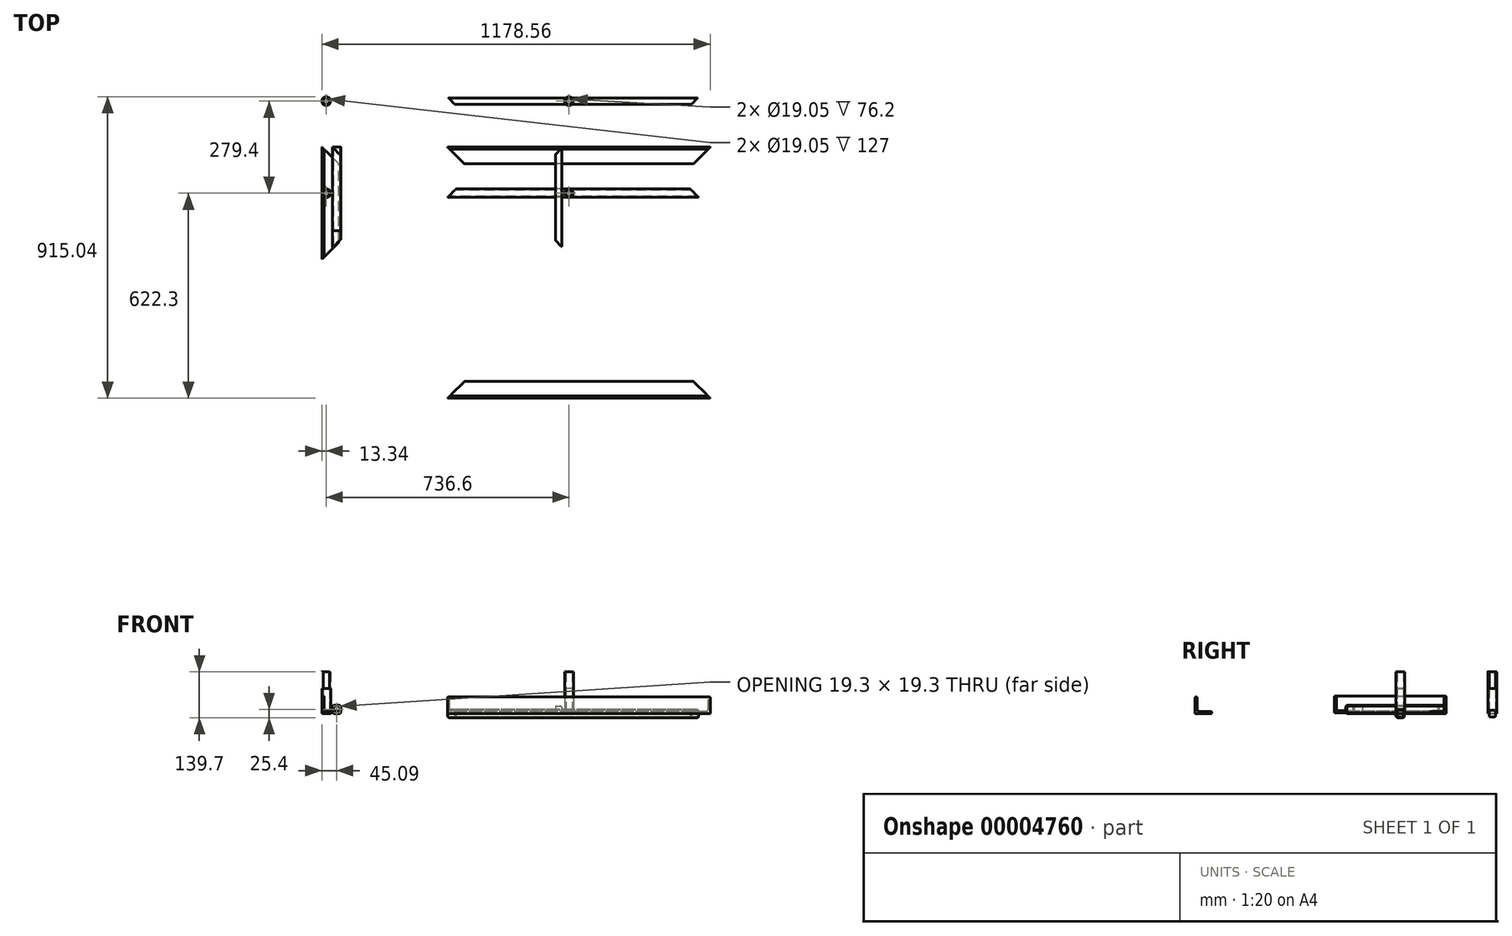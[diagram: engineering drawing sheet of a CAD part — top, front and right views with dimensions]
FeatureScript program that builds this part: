
annotation { "Feature Type Name" : "Feature", "Feature Type Description" : "" }
export const myFeature = defineFeature(function(context is Context, id is Id, definition is map)
    precondition{}
    {
        {
            var Q0;
            Q0=qCreatedBy(makeId("Front.planeOp"),FACE);
            var sketch = newSketch(context, id + "F0", { "sketchPlane" : qUnion([Q0])});
            skLineSegment(sketch, "E0", {"start": v(-381, 50.18) * mm, "end": v(-381, 2.55) * mm});
            skLineSegment(sketch, "E1", {"start": v(-381, 2.55) * mm, "end": v(-333.38, 2.55) * mm});
            skLineSegment(sketch, "E2.0", {"start": v(-368.3, 8.9) * mm, "end": v(-333.38, 8.9) * mm});
            skLineSegment(sketch, "E2.1", {"start": v(-374.65, 50.18) * mm, "end": v(-374.65, 15.25) * mm});
            skArc(sketch, "E3", {"start": v(-374.65, 50.18) * mm, "mid": v(-377.83, 53.35) * mm, "end": v(-381, 50.18) * mm});
            skArc(sketch, "E4", {"start": v(-333.38, 2.55) * mm, "mid": v(-330.2, 5.73) * mm, "end": v(-333.38, 8.9) * mm});
            skPoint(sketch, "E5.visualSharp", {"position": v(-374.65, 8.9) * mm});
            skArc(sketch, "E5.filletArc", {"start": v(-374.65, 15.25) * mm, "mid": v(-372.8, 10.76) * mm, "end": v(-368.3, 8.9) * mm});
            skArc(sketch, "E6.MirrorCS", {"start": v(374.65, 50.18) * mm, "mid": v(377.83, 53.35) * mm, "end": v(381, 50.18) * mm});
            skLineSegment(sketch, "E7.MirrorCS", {"start": v(374.65, 50.18) * mm, "end": v(374.65, 15.25) * mm});
            skArc(sketch, "E8.MirrorCS", {"start": v(374.65, 15.25) * mm, "mid": v(372.8, 10.76) * mm, "end": v(368.3, 8.9) * mm});
            skLineSegment(sketch, "E9.MirrorCS", {"start": v(368.3, 8.9) * mm, "end": v(333.38, 8.9) * mm});
            skArc(sketch, "E10.MirrorCS", {"start": v(333.38, 2.55) * mm, "mid": v(330.2, 5.73) * mm, "end": v(333.38, 8.9) * mm});
            skLineSegment(sketch, "E11.MirrorCS", {"start": v(381, 2.55) * mm, "end": v(333.38, 2.55) * mm});
            skLineSegment(sketch, "E12.MirrorCS", {"start": v(381, 50.18) * mm, "end": v(381, 2.55) * mm});
            skSolve(sketch);
        }
        {
            var Q0;
            Q0=makeQuery(id+"F0.imprint","IMPRINT",FACE,{"disambiguationData":[TD([[makeQuery(id+"F0.imprint","IMPRINT",EDGE,{"derivedFrom":sQuery(id+"F0.wireOp",EDGE,"E6.MirrorCS")}),-1.0]])]});
            var Q1;
            Q1=makeQuery(id+"F0.imprint","IMPRINT",FACE,{"disambiguationData":[TD([[makeQuery(id+"F0.imprint","IMPRINT",EDGE,{"derivedFrom":sQuery(id+"F0.wireOp",EDGE,"E0")}),1.0]])]});
            extrude(context, id + "F1", {"entities" : qUnion([Q0, Q1]), "depth" : 339.72 * mm, "offsetDistance" : 25.4 * mm});
        }
        {
            var Q0;
            Q0=qCreatedBy(makeId("Top.planeOp"),FACE);
            var sketch = newSketch(context, id + "F2", { "sketchPlane" : qUnion([Q0])});
            skLineSegment(sketch, "E13.0", {"start": v(-381, 0) * mm, "end": v(-333.38, 0) * mm});
            skLineSegment(sketch, "E14.0", {"start": v(-381, -339.73) * mm, "end": v(-333.38, -339.73) * mm});
            skLineSegment(sketch, "E15.0", {"start": v(381, -339.73) * mm, "end": v(333.38, -339.73) * mm});
            skLineSegment(sketch, "E16.0", {"start": v(381, 0) * mm, "end": v(333.38, 0) * mm});
            skLineSegment(sketch, "E17", {"start": v(-327.12, -53.88) * mm, "end": v(-381, 0) * mm});
            skLineSegment(sketch, "E18", {"start": v(-327.12, -285.84) * mm, "end": v(-381, -339.73) * mm});
            skLineSegment(sketch, "E19", {"start": v(-333.38, 0) * mm, "end": v(-236.74, 0) * mm});
            skLineSegment(sketch, "E20", {"start": v(-236.74, 0) * mm, "end": v(-327.12, -53.88) * mm});
            skLineSegment(sketch, "E21", {"start": v(-333.38, -339.73) * mm, "end": v(-245.08, -339.73) * mm});
            skLineSegment(sketch, "E22", {"start": v(-245.08, -339.73) * mm, "end": v(-327.12, -285.84) * mm});
            skLineSegment(sketch, "E23", {"start": v(381, 0) * mm, "end": v(311.3, -69.7) * mm});
            skLineSegment(sketch, "E24", {"start": v(381, -339.73) * mm, "end": v(294.62, -253.35) * mm});
            skLineSegment(sketch, "E25", {"start": v(333.38, 0) * mm, "end": v(172.94, 0) * mm});
            skLineSegment(sketch, "E26", {"start": v(172.94, 0) * mm, "end": v(311.3, -69.7) * mm});
            skLineSegment(sketch, "E27", {"start": v(333.38, -339.73) * mm, "end": v(187.89, -339.73) * mm});
            skLineSegment(sketch, "E28", {"start": v(187.89, -339.73) * mm, "end": v(294.62, -253.35) * mm});
            skSolve(sketch);
        }
        {
            var Q0;
            Q0=makeQuery(id+"F2.imprint","IMPRINT",FACE,{"disambiguationData":[TD([[makeQuery(id+"F2.imprint","IMPRINT",EDGE,{"derivedFrom":sQuery(id+"F2.wireOp",EDGE,"E14.0")}),1.0]])]});
            var Q1;
            Q1=makeQuery(id+"F2.imprint","IMPRINT",FACE,{"disambiguationData":[TD([[makeQuery(id+"F2.imprint","IMPRINT",EDGE,{"derivedFrom":sQuery(id+"F2.wireOp",EDGE,"E13.0")}),-1.0]])]});
            var Q2;
            Q2=makeQuery(id+"F2.imprint","IMPRINT",FACE,{"disambiguationData":[TD([[makeQuery(id+"F2.imprint","IMPRINT",EDGE,{"derivedFrom":sQuery(id+"F2.wireOp",EDGE,"E16.0")}),1.0]])]});
            var Q3;
            Q3=makeQuery(id+"F2.imprint","IMPRINT",FACE,{"disambiguationData":[TD([[makeQuery(id+"F2.imprint","IMPRINT",EDGE,{"derivedFrom":sQuery(id+"F2.wireOp",EDGE,"E15.0")}),-1.0]])]});
            extrude(context, id + "F3", {"entities" : qUnion([Q0, Q1, Q2, Q3]), "depth" : 76.2 * mm, "offsetDistance" : 25.4 * mm});
        }
        {
            var Q0;
            Q0=makeQuery(id+"F3.opExtrude","SWEPT_BODY",BODY,{"disambiguationData":[OSD([sQuery(id+"F2.wireOp",EDGE,"E13.0"),sQuery(id+"F2.wireOp",EDGE,"E17"),sQuery(id+"F2.wireOp",EDGE,"E19"),sQuery(id+"F2.wireOp",EDGE,"E20")])]});
            var Q1;
            Q1=makeQuery(id+"F3.opExtrude","SWEPT_BODY",BODY,{"disambiguationData":[OSD([sQuery(id+"F2.wireOp",EDGE,"E14.0"),sQuery(id+"F2.wireOp",EDGE,"E18"),sQuery(id+"F2.wireOp",EDGE,"E21"),sQuery(id+"F2.wireOp",EDGE,"E22")])]});
            var Q2;
            Q2=makeQuery(id+"F3.opExtrude","SWEPT_BODY",BODY,{"disambiguationData":[OSD([sQuery(id+"F2.wireOp",EDGE,"E16.0"),sQuery(id+"F2.wireOp",EDGE,"E23"),sQuery(id+"F2.wireOp",EDGE,"E25"),sQuery(id+"F2.wireOp",EDGE,"E26")])]});
            var Q3;
            Q3=makeQuery(id+"F3.opExtrude","SWEPT_BODY",BODY,{"disambiguationData":[OSD([sQuery(id+"F2.wireOp",EDGE,"E15.0"),sQuery(id+"F2.wireOp",EDGE,"E24"),sQuery(id+"F2.wireOp",EDGE,"E27"),sQuery(id+"F2.wireOp",EDGE,"E28")])]});
            var Q4;
            Q4=makeQuery(id+"F1.opExtrude","SWEPT_BODY",BODY,{"disambiguationData":[OSD([sQuery(id+"F0.wireOp",EDGE,"E0"),sQuery(id+"F0.wireOp",EDGE,"E1"),sQuery(id+"F0.wireOp",EDGE,"E2.0"),sQuery(id+"F0.wireOp",EDGE,"E2.1"),sQuery(id+"F0.wireOp",EDGE,"E3"),sQuery(id+"F0.wireOp",EDGE,"E4"),sQuery(id+"F0.wireOp",EDGE,"E5.filletArc")])]});
            var Q5;
            Q5=makeQuery(id+"F1.opExtrude","SWEPT_BODY",BODY,{"disambiguationData":[OSD([sQuery(id+"F0.wireOp",EDGE,"E6.MirrorCS"),sQuery(id+"F0.wireOp",EDGE,"E7.MirrorCS"),sQuery(id+"F0.wireOp",EDGE,"E8.MirrorCS"),sQuery(id+"F0.wireOp",EDGE,"E9.MirrorCS"),sQuery(id+"F0.wireOp",EDGE,"E10.MirrorCS"),sQuery(id+"F0.wireOp",EDGE,"E11.MirrorCS"),sQuery(id+"F0.wireOp",EDGE,"E12.MirrorCS")])]});
            booleanBodies(context, id + "F4", {"operationType" : BooleanOperationType.SUBTRACTION, "tools" : qUnion([Q0, Q1, Q2, Q3]), "targets" : qUnion([Q4, Q5])});
        }
        {
            var Q0;
            Q0=qCreatedBy(makeId("Right.planeOp"),FACE);
            var sketch = newSketch(context, id + "F5", { "sketchPlane" : qUnion([Q0])});
            skLineSegment(sketch, "E29", {"start": v(-762, 47.62) * mm, "end": v(-762, 0) * mm});
            skLineSegment(sketch, "E30", {"start": v(-762, 0) * mm, "end": v(-714.38, 0) * mm});
            skLineSegment(sketch, "E31.0", {"start": v(-749.3, 6.35) * mm, "end": v(-714.38, 6.35) * mm});
            skLineSegment(sketch, "E31.1", {"start": v(-755.65, 47.62) * mm, "end": v(-755.65, 12.7) * mm});
            skArc(sketch, "E32", {"start": v(-755.65, 47.62) * mm, "mid": v(-758.83, 50.8) * mm, "end": v(-762, 47.62) * mm});
            skArc(sketch, "E33", {"start": v(-714.38, 0) * mm, "mid": v(-711.2, 3.17) * mm, "end": v(-714.38, 6.35) * mm});
            skPoint(sketch, "E34.visualSharp", {"position": v(-755.65, 6.35) * mm});
            skArc(sketch, "E34.filletArc", {"start": v(-755.65, 12.7) * mm, "mid": v(-753.8, 8.2) * mm, "end": v(-749.3, 6.35) * mm});
            skLineSegment(sketch, "E35", {"start": v(-47.63, 0) * mm, "end": v(0, 0) * mm});
            skLineSegment(sketch, "E36", {"start": v(0, 0) * mm, "end": v(0, 47.62) * mm});
            skLineSegment(sketch, "E37.0", {"start": v(-6.35, 12.7) * mm, "end": v(-6.35, 47.62) * mm});
            skLineSegment(sketch, "E37.1", {"start": v(-47.63, 6.35) * mm, "end": v(-12.7, 6.35) * mm});
            skArc(sketch, "E38", {"start": v(-47.63, 6.35) * mm, "mid": v(-50.8, 3.17) * mm, "end": v(-47.63, 0) * mm});
            skArc(sketch, "E39", {"start": v(0, 47.62) * mm, "mid": v(-3.18, 50.8) * mm, "end": v(-6.35, 47.62) * mm});
            skPoint(sketch, "E40.visualSharp", {"position": v(-6.35, 6.35) * mm});
            skArc(sketch, "E40.filletArc", {"start": v(-12.7, 6.35) * mm, "mid": v(-8.2, 8.2) * mm, "end": v(-6.35, 12.7) * mm});
            skSolve(sketch);
        }
        {
            var Q0;
            Q0=makeQuery(id+"F5.imprint","IMPRINT",FACE,{"disambiguationData":[TD([[makeQuery(id+"F5.imprint","IMPRINT",EDGE,{"derivedFrom":sQuery(id+"F5.wireOp",EDGE,"E29")}),1.0]])]});
            var Q1;
            Q1=makeQuery(id+"F5.imprint","IMPRINT",FACE,{"disambiguationData":[TD([[makeQuery(id+"F5.imprint","IMPRINT",EDGE,{"derivedFrom":sQuery(id+"F5.wireOp",EDGE,"E35")}),1.0]])]});
            extrude(context, id + "F6", {"entities" : qUnion([Q0, Q1]), "depth" : 796.92 * mm, "offsetDistance" : 25.4 * mm});
        }
        {
            var Q0;
            Q0=qCreatedBy(makeId("Top.planeOp"),FACE);
            var sketch = newSketch(context, id + "F7", { "sketchPlane" : qUnion([Q0])});
            skLineSegment(sketch, "E41.0", {"start": v(796.93, -47.63) * mm, "end": v(796.93, 0) * mm});
            skLineSegment(sketch, "E42.0", {"start": v(796.93, -762) * mm, "end": v(796.93, -714.38) * mm});
            skLineSegment(sketch, "E43.0", {"start": v(0, -762) * mm, "end": v(0, -714.38) * mm});
            skLineSegment(sketch, "E44.0", {"start": v(0, -47.63) * mm, "end": v(0, 0) * mm});
            skLineSegment(sketch, "E45", {"start": v(0, 0) * mm, "end": v(70.95, -70.95) * mm});
            skLineSegment(sketch, "E46", {"start": v(796.93, 0) * mm, "end": v(711.06, -85.86) * mm});
            skLineSegment(sketch, "E47", {"start": v(0, -47.63) * mm, "end": v(0, -70.95) * mm});
            skLineSegment(sketch, "E48", {"start": v(0, -70.95) * mm, "end": v(70.95, -70.95) * mm});
            skLineSegment(sketch, "E49", {"start": v(796.93, -47.63) * mm, "end": v(796.93, -85.86) * mm});
            skLineSegment(sketch, "E50", {"start": v(796.93, -85.86) * mm, "end": v(711.06, -85.86) * mm});
            skLineSegment(sketch, "E51", {"start": v(0, -762) * mm, "end": v(84.63, -677.37) * mm});
            skLineSegment(sketch, "E52", {"start": v(796.93, -762) * mm, "end": v(712.97, -678.04) * mm});
            skLineSegment(sketch, "E53", {"start": v(0, -714.38) * mm, "end": v(0, -677.37) * mm});
            skLineSegment(sketch, "E54", {"start": v(0, -677.37) * mm, "end": v(84.63, -677.37) * mm});
            skLineSegment(sketch, "E55", {"start": v(796.93, -714.38) * mm, "end": v(796.93, -678.04) * mm});
            skLineSegment(sketch, "E56", {"start": v(796.93, -678.04) * mm, "end": v(712.97, -678.04) * mm});
            skSolve(sketch);
        }
        {
            var Q0;
            Q0=makeQuery(id+"F7.imprint","IMPRINT",FACE,{"disambiguationData":[TD([[makeQuery(id+"F7.imprint","IMPRINT",EDGE,{"derivedFrom":sQuery(id+"F7.wireOp",EDGE,"E44.0")}),-1.0]])]});
            var Q1;
            Q1=makeQuery(id+"F7.imprint","IMPRINT",FACE,{"disambiguationData":[TD([[makeQuery(id+"F7.imprint","IMPRINT",EDGE,{"derivedFrom":sQuery(id+"F7.wireOp",EDGE,"E41.0")}),1.0]])]});
            var Q2;
            Q2=makeQuery(id+"F7.imprint","IMPRINT",FACE,{"disambiguationData":[TD([[makeQuery(id+"F7.imprint","IMPRINT",EDGE,{"derivedFrom":sQuery(id+"F7.wireOp",EDGE,"E43.0")}),-1.0]])]});
            var Q3;
            Q3=makeQuery(id+"F7.imprint","IMPRINT",FACE,{"disambiguationData":[TD([[makeQuery(id+"F7.imprint","IMPRINT",EDGE,{"derivedFrom":sQuery(id+"F7.wireOp",EDGE,"E42.0")}),1.0]])]});
            extrude(context, id + "F8", {"entities" : qUnion([Q0, Q1, Q2, Q3]), "depth" : 76.2 * mm, "offsetDistance" : 25.4 * mm});
        }
        {
            var Q0;
            Q0=makeQuery(id+"F8.opExtrude","SWEPT_BODY",BODY,{"disambiguationData":[OSD([sQuery(id+"F7.wireOp",EDGE,"E44.0"),sQuery(id+"F7.wireOp",EDGE,"E45"),sQuery(id+"F7.wireOp",EDGE,"E47"),sQuery(id+"F7.wireOp",EDGE,"E48")])]});
            var Q1;
            Q1=makeQuery(id+"F8.opExtrude","SWEPT_BODY",BODY,{"disambiguationData":[OSD([sQuery(id+"F7.wireOp",EDGE,"E41.0"),sQuery(id+"F7.wireOp",EDGE,"E46"),sQuery(id+"F7.wireOp",EDGE,"E49"),sQuery(id+"F7.wireOp",EDGE,"E50")])]});
            var Q2;
            Q2=makeQuery(id+"F8.opExtrude","SWEPT_BODY",BODY,{"disambiguationData":[OSD([sQuery(id+"F7.wireOp",EDGE,"E43.0"),sQuery(id+"F7.wireOp",EDGE,"E51"),sQuery(id+"F7.wireOp",EDGE,"E53"),sQuery(id+"F7.wireOp",EDGE,"E54")])]});
            var Q3;
            Q3=makeQuery(id+"F8.opExtrude","SWEPT_BODY",BODY,{"disambiguationData":[OSD([sQuery(id+"F7.wireOp",EDGE,"E42.0"),sQuery(id+"F7.wireOp",EDGE,"E52"),sQuery(id+"F7.wireOp",EDGE,"E55"),sQuery(id+"F7.wireOp",EDGE,"E56")])]});
            var Q4;
            Q4=makeQuery(id+"F6.opExtrude","SWEPT_BODY",BODY,{"disambiguationData":[OSD([sQuery(id+"F5.wireOp",EDGE,"E35"),sQuery(id+"F5.wireOp",EDGE,"E36"),sQuery(id+"F5.wireOp",EDGE,"E37.0"),sQuery(id+"F5.wireOp",EDGE,"E37.1"),sQuery(id+"F5.wireOp",EDGE,"E38"),sQuery(id+"F5.wireOp",EDGE,"E39"),sQuery(id+"F5.wireOp",EDGE,"E40.filletArc")])]});
            var Q5;
            Q5=makeQuery(id+"F6.opExtrude","SWEPT_BODY",BODY,{"disambiguationData":[OSD([sQuery(id+"F5.wireOp",EDGE,"E29"),sQuery(id+"F5.wireOp",EDGE,"E30"),sQuery(id+"F5.wireOp",EDGE,"E31.0"),sQuery(id+"F5.wireOp",EDGE,"E31.1"),sQuery(id+"F5.wireOp",EDGE,"E32"),sQuery(id+"F5.wireOp",EDGE,"E33"),sQuery(id+"F5.wireOp",EDGE,"E34.filletArc")])]});
            booleanBodies(context, id + "F9", {"operationType" : BooleanOperationType.SUBTRACTION, "tools" : qUnion([Q0, Q1, Q2, Q3]), "targets" : qUnion([Q4, Q5])});
        }
        {
            var Q0;
            Q0=qCreatedBy(makeId("Front.planeOp"),FACE);
            var sketch = newSketch(context, id + "F10", { "sketchPlane" : qUnion([Q0])});
            skLineSegment(sketch, "E57.bottom", {"start": v(-329.95, 25.4) * mm, "end": v(-343.15, 25.4) * mm});
            skLineSegment(sketch, "E57.top", {"start": v(-329.95, 0) * mm, "end": v(-343.15, 0) * mm});
            skLineSegment(sketch, "E57.left", {"start": v(-323.85, 19.3) * mm, "end": v(-323.85, 6.1) * mm});
            skLineSegment(sketch, "E57.right", {"start": v(-349.25, 19.3) * mm, "end": v(-349.25, 6.1) * mm});
            skPoint(sketch, "E57.middle", {"position": v(-336.55, 12.7) * mm});
            skPoint(sketch, "E58.visualSharp", {"position": v(-349.25, 25.4) * mm});
            skArc(sketch, "E58.filletArc", {"start": v(-343.15, 25.4) * mm, "mid": v(-347.46, 23.61) * mm, "end": v(-349.25, 19.3) * mm});
            skPoint(sketch, "E59.visualSharp", {"position": v(-323.85, 25.4) * mm});
            skArc(sketch, "E59.filletArc", {"start": v(-323.85, 19.3) * mm, "mid": v(-325.64, 23.61) * mm, "end": v(-329.95, 25.4) * mm});
            skPoint(sketch, "E60.visualSharp", {"position": v(-323.85, 0) * mm});
            skArc(sketch, "E60.filletArc", {"start": v(-329.95, 0) * mm, "mid": v(-325.64, 1.79) * mm, "end": v(-323.85, 6.1) * mm});
            skPoint(sketch, "E61.visualSharp", {"position": v(-349.25, 0) * mm});
            skArc(sketch, "E61.filletArc", {"start": v(-349.25, 6.1) * mm, "mid": v(-347.46, 1.79) * mm, "end": v(-343.15, 0) * mm});
            skArc(sketch, "E62.0", {"start": v(-326.9, 19.3) * mm, "mid": v(-327.8, 21.46) * mm, "end": v(-329.95, 22.35) * mm});
            skLineSegment(sketch, "E62.1", {"start": v(-326.9, 19.3) * mm, "end": v(-326.9, 6.1) * mm});
            skLineSegment(sketch, "E62.2", {"start": v(-329.95, 22.35) * mm, "end": v(-343.15, 22.35) * mm});
            skArc(sketch, "E62.3", {"start": v(-329.95, 3.05) * mm, "mid": v(-327.8, 3.94) * mm, "end": v(-326.9, 6.1) * mm});
            skArc(sketch, "E62.4", {"start": v(-343.15, 22.35) * mm, "mid": v(-345.3, 21.46) * mm, "end": v(-346.2, 19.3) * mm});
            skLineSegment(sketch, "E62.5", {"start": v(-346.2, 19.3) * mm, "end": v(-346.2, 6.1) * mm});
            skArc(sketch, "E62.6", {"start": v(-346.2, 6.1) * mm, "mid": v(-345.3, 3.94) * mm, "end": v(-343.15, 3.05) * mm});
            skLineSegment(sketch, "E62.7", {"start": v(-329.95, 3.05) * mm, "end": v(-343.15, 3.05) * mm});
            skLineSegment(sketch, "E63", {"start": v(0, 42.38) * mm, "end": v(0, -25.41) * mm});
            skPoint(sketch, "E64", {"position": v(0, 0) * mm});
            skArc(sketch, "E65.MirrorCS", {"start": v(346.2, 6.1) * mm, "mid": v(345.3, 3.94) * mm, "end": v(343.15, 3.05) * mm});
            skArc(sketch, "E66.MirrorCS", {"start": v(329.95, 3.05) * mm, "mid": v(327.8, 3.94) * mm, "end": v(326.9, 6.1) * mm});
            skArc(sketch, "E67.MirrorCS", {"start": v(326.9, 19.3) * mm, "mid": v(327.8, 21.46) * mm, "end": v(329.95, 22.35) * mm});
            skArc(sketch, "E68.MirrorCS", {"start": v(343.15, 22.35) * mm, "mid": v(345.3, 21.46) * mm, "end": v(346.2, 19.3) * mm});
            skArc(sketch, "E69.MirrorCS", {"start": v(323.85, 19.3) * mm, "mid": v(325.64, 23.61) * mm, "end": v(329.95, 25.4) * mm});
            skLineSegment(sketch, "E70.MirrorCS", {"start": v(329.95, 22.35) * mm, "end": v(343.15, 22.35) * mm});
            skLineSegment(sketch, "E71.MirrorCS", {"start": v(329.95, 25.4) * mm, "end": v(343.15, 25.4) * mm});
            skArc(sketch, "E72.MirrorCS", {"start": v(349.25, 6.1) * mm, "mid": v(347.46, 1.79) * mm, "end": v(343.15, 0) * mm});
            skLineSegment(sketch, "E73.MirrorCS", {"start": v(329.95, 3.05) * mm, "end": v(343.15, 3.05) * mm});
            skArc(sketch, "E74.MirrorCS", {"start": v(329.95, 0) * mm, "mid": v(325.64, 1.79) * mm, "end": v(323.85, 6.1) * mm});
            skArc(sketch, "E75.MirrorCS", {"start": v(343.15, 25.4) * mm, "mid": v(347.46, 23.61) * mm, "end": v(349.25, 19.3) * mm});
            skLineSegment(sketch, "E76.MirrorCS", {"start": v(329.95, 0) * mm, "end": v(343.15, 0) * mm});
            skPoint(sketch, "E77.MirrorP", {"position": v(349.25, 0) * mm});
            skLineSegment(sketch, "E78.MirrorCS", {"start": v(349.25, 19.3) * mm, "end": v(349.25, 6.1) * mm});
            skPoint(sketch, "E79.MirrorP", {"position": v(336.55, 12.7) * mm});
            skLineSegment(sketch, "E80.MirrorCS", {"start": v(346.2, 19.3) * mm, "end": v(346.2, 6.1) * mm});
            skLineSegment(sketch, "E81.MirrorCS", {"start": v(323.85, 19.3) * mm, "end": v(323.85, 6.1) * mm});
            skPoint(sketch, "E82.MirrorP", {"position": v(323.85, 0) * mm});
            skLineSegment(sketch, "E83.MirrorCS", {"start": v(326.9, 19.3) * mm, "end": v(326.9, 6.1) * mm});
            skPoint(sketch, "E84.MirrorP", {"position": v(349.25, 25.4) * mm});
            skPoint(sketch, "E85.MirrorP", {"position": v(323.85, 25.4) * mm});
            skSolve(sketch);
        }
        {
            var Q0;
            Q0=makeQuery(id+"F10.imprint","IMPRINT",FACE,{"disambiguationData":[TD([[makeQuery(id+"F10.imprint","IMPRINT",EDGE,{"derivedFrom":sQuery(id+"F10.wireOp",EDGE,"E57.bottom")}),1.0]])]});
            var Q1;
            Q1=makeQuery(id+"F10.imprint","IMPRINT",FACE,{"disambiguationData":[TD([[makeQuery(id+"F10.imprint","IMPRINT",EDGE,{"derivedFrom":sQuery(id+"F10.wireOp",EDGE,"E65.MirrorCS")}),1.0]])]});
            extrude(context, id + "F11", {"entities" : qUnion([Q0, Q1]), "depth" : 304.8 * mm, "offsetDistance" : 25.4 * mm});
        }
        {
            var Q0;
            Q0=qCreatedBy(makeId("Top.planeOp"),FACE);
            var sketch = newSketch(context, id + "F12", { "sketchPlane" : qUnion([Q0])});
            skLineSegment(sketch, "E86.0", {"start": v(-323.85, -304.8) * mm, "end": v(-349.25, -304.8) * mm});
            skLineSegment(sketch, "E86.1", {"start": v(-349.25, -304.8) * mm, "end": v(-323.85, -279.4) * mm});
            skLineSegment(sketch, "E86.2", {"start": v(-323.85, -279.4) * mm, "end": v(-323.85, -304.8) * mm});
            skPoint(sketch, "E86.0.midPoint", {"position": v(-336.55, -304.8) * mm});
            skPoint(sketch, "E87", {"position": v(-323.85, -292.1) * mm});
            skLineSegment(sketch, "E88.0", {"start": v(-323.85, 0) * mm, "end": v(-323.85, -25.4) * mm});
            skLineSegment(sketch, "E88.1", {"start": v(-323.85, -25.4) * mm, "end": v(-349.25, 0) * mm});
            skLineSegment(sketch, "E88.2", {"start": v(-349.25, 0) * mm, "end": v(-323.85, 0) * mm});
            skPoint(sketch, "E88.0.midPoint", {"position": v(-323.85, -12.7) * mm});
            skPoint(sketch, "E89", {"position": v(-336.55, 0) * mm});
            skLineSegment(sketch, "E90.MirrorCS", {"start": v(323.85, 0) * mm, "end": v(323.85, -25.4) * mm});
            skLineSegment(sketch, "E91.MirrorCS", {"start": v(323.85, -304.8) * mm, "end": v(349.25, -304.8) * mm});
            skLineSegment(sketch, "E92.MirrorCS", {"start": v(323.85, -279.4) * mm, "end": v(323.85, -304.8) * mm});
            skLineSegment(sketch, "E93.MirrorCS", {"start": v(349.25, 0) * mm, "end": v(323.85, 0) * mm});
            skPoint(sketch, "E94.MirrorP", {"position": v(323.85, -12.7) * mm});
            skPoint(sketch, "E95.MirrorP", {"position": v(323.85, -292.1) * mm});
            skLineSegment(sketch, "E96.MirrorCS", {"start": v(323.85, -25.4) * mm, "end": v(349.25, 0) * mm});
            skPoint(sketch, "E97.MirrorP", {"position": v(336.55, 0) * mm});
            skLineSegment(sketch, "E98.MirrorCS", {"start": v(349.25, -304.8) * mm, "end": v(323.85, -279.4) * mm});
            skPoint(sketch, "E99.MirrorP", {"position": v(336.55, -304.8) * mm});
            skSolve(sketch);
        }
        {
            var Q0;
            Q0=makeQuery(id+"F12.imprint","IMPRINT",FACE,{"disambiguationData":[TD([[makeQuery(id+"F12.imprint","IMPRINT",EDGE,{"derivedFrom":sQuery(id+"F12.wireOp",EDGE,"E86.0")}),-1.0]])]});
            var Q1;
            Q1=makeQuery(id+"F12.imprint","IMPRINT",FACE,{"disambiguationData":[TD([[makeQuery(id+"F12.imprint","IMPRINT",EDGE,{"derivedFrom":sQuery(id+"F12.wireOp",EDGE,"E91.MirrorCS")}),1.0]])]});
            var Q2;
            Q2=makeQuery(id+"F12.imprint","IMPRINT",FACE,{"disambiguationData":[TD([[makeQuery(id+"F12.imprint","IMPRINT",EDGE,{"derivedFrom":sQuery(id+"F12.wireOp",EDGE,"E90.MirrorCS")}),1.0]])]});
            var Q3;
            Q3=makeQuery(id+"F12.imprint","IMPRINT",FACE,{"disambiguationData":[TD([[makeQuery(id+"F12.imprint","IMPRINT",EDGE,{"derivedFrom":sQuery(id+"F12.wireOp",EDGE,"E88.0")}),-1.0]])]});
            extrude(context, id + "F13", {"entities" : qUnion([Q0, Q1, Q2, Q3]), "depth" : 76.2 * mm, "offsetDistance" : 25.4 * mm});
        }
        {
            var Q0;
            Q0=makeQuery(id+"F13.opExtrude","SWEPT_BODY",BODY,{"disambiguationData":[OSD([sQuery(id+"F12.wireOp",EDGE,"E90.MirrorCS"),sQuery(id+"F12.wireOp",EDGE,"E93.MirrorCS"),sQuery(id+"F12.wireOp",EDGE,"E96.MirrorCS")])]});
            var Q1;
            Q1=makeQuery(id+"F13.opExtrude","SWEPT_BODY",BODY,{"disambiguationData":[OSD([sQuery(id+"F12.wireOp",EDGE,"E91.MirrorCS"),sQuery(id+"F12.wireOp",EDGE,"E92.MirrorCS"),sQuery(id+"F12.wireOp",EDGE,"E98.MirrorCS")])]});
            var Q2;
            Q2=makeQuery(id+"F13.opExtrude","SWEPT_BODY",BODY,{"disambiguationData":[OSD([sQuery(id+"F12.wireOp",EDGE,"E86.0"),sQuery(id+"F12.wireOp",EDGE,"E86.1"),sQuery(id+"F12.wireOp",EDGE,"E86.2")])]});
            var Q3;
            Q3=makeQuery(id+"F13.opExtrude","SWEPT_BODY",BODY,{"disambiguationData":[OSD([sQuery(id+"F12.wireOp",EDGE,"E88.0"),sQuery(id+"F12.wireOp",EDGE,"E88.1"),sQuery(id+"F12.wireOp",EDGE,"E88.2")])]});
            var Q4;
            Q4=makeQuery(id+"F11.opExtrude","SWEPT_BODY",BODY,{"disambiguationData":[OSD([sQuery(id+"F10.wireOp",EDGE,"E57.bottom"),sQuery(id+"F10.wireOp",EDGE,"E57.top"),sQuery(id+"F10.wireOp",EDGE,"E57.left"),sQuery(id+"F10.wireOp",EDGE,"E57.right"),sQuery(id+"F10.wireOp",EDGE,"E58.filletArc"),sQuery(id+"F10.wireOp",EDGE,"E59.filletArc"),sQuery(id+"F10.wireOp",EDGE,"E60.filletArc"),sQuery(id+"F10.wireOp",EDGE,"E61.filletArc"),sQuery(id+"F10.wireOp",EDGE,"E62.0"),sQuery(id+"F10.wireOp",EDGE,"E62.1"),sQuery(id+"F10.wireOp",EDGE,"E62.2"),sQuery(id+"F10.wireOp",EDGE,"E62.3"),sQuery(id+"F10.wireOp",EDGE,"E62.4"),sQuery(id+"F10.wireOp",EDGE,"E62.5"),sQuery(id+"F10.wireOp",EDGE,"E62.6"),sQuery(id+"F10.wireOp",EDGE,"E62.7")])]});
            var Q5;
            Q5=makeQuery(id+"F11.opExtrude","SWEPT_BODY",BODY,{"disambiguationData":[OSD([sQuery(id+"F10.wireOp",EDGE,"E65.MirrorCS"),sQuery(id+"F10.wireOp",EDGE,"E66.MirrorCS"),sQuery(id+"F10.wireOp",EDGE,"E67.MirrorCS"),sQuery(id+"F10.wireOp",EDGE,"E68.MirrorCS"),sQuery(id+"F10.wireOp",EDGE,"E69.MirrorCS"),sQuery(id+"F10.wireOp",EDGE,"E70.MirrorCS"),sQuery(id+"F10.wireOp",EDGE,"E71.MirrorCS"),sQuery(id+"F10.wireOp",EDGE,"E72.MirrorCS"),sQuery(id+"F10.wireOp",EDGE,"E73.MirrorCS"),sQuery(id+"F10.wireOp",EDGE,"E74.MirrorCS"),sQuery(id+"F10.wireOp",EDGE,"E75.MirrorCS"),sQuery(id+"F10.wireOp",EDGE,"E76.MirrorCS"),sQuery(id+"F10.wireOp",EDGE,"E78.MirrorCS"),sQuery(id+"F10.wireOp",EDGE,"E80.MirrorCS"),sQuery(id+"F10.wireOp",EDGE,"E81.MirrorCS"),sQuery(id+"F10.wireOp",EDGE,"E83.MirrorCS")])]});
            booleanBodies(context, id + "F14", {"operationType" : BooleanOperationType.SUBTRACTION, "tools" : qUnion([Q0, Q1, Q2, Q3]), "targets" : qUnion([Q4, Q5])});
        }
        {
            var Q0;
            Q0=qCreatedBy(makeId("Right.planeOp"),FACE);
            var sketch = newSketch(context, id + "F15", { "sketchPlane" : qUnion([Q0])});
            skLineSegment(sketch, "E100.bottom", {"start": v(-133.1, 12.7) * mm, "end": v(-146.3, 12.7) * mm});
            skLineSegment(sketch, "E100.top", {"start": v(-133.1, -12.7) * mm, "end": v(-146.3, -12.7) * mm});
            skLineSegment(sketch, "E100.left", {"start": v(-127, 6.6) * mm, "end": v(-127, -6.6) * mm});
            skLineSegment(sketch, "E100.right", {"start": v(-152.4, 6.6) * mm, "end": v(-152.4, -6.6) * mm});
            skPoint(sketch, "E100.middle", {"position": v(-139.7, 0) * mm});
            skPoint(sketch, "E101.visualSharp", {"position": v(-152.4, 12.7) * mm});
            skArc(sketch, "E101.filletArc", {"start": v(-146.3, 12.7) * mm, "mid": v(-150.61, 10.91) * mm, "end": v(-152.4, 6.6) * mm});
            skPoint(sketch, "E102.visualSharp", {"position": v(-127, 12.7) * mm});
            skArc(sketch, "E102.filletArc", {"start": v(-127, 6.6) * mm, "mid": v(-128.79, 10.91) * mm, "end": v(-133.1, 12.7) * mm});
            skPoint(sketch, "E103.visualSharp", {"position": v(-127, -12.7) * mm});
            skArc(sketch, "E103.filletArc", {"start": v(-133.1, -12.7) * mm, "mid": v(-128.79, -10.91) * mm, "end": v(-127, -6.6) * mm});
            skPoint(sketch, "E104.visualSharp", {"position": v(-152.4, -12.7) * mm});
            skArc(sketch, "E104.filletArc", {"start": v(-152.4, -6.6) * mm, "mid": v(-150.61, -10.91) * mm, "end": v(-146.3, -12.7) * mm});
            skArc(sketch, "E105.0", {"start": v(-130.05, 6.6) * mm, "mid": v(-130.94, 8.76) * mm, "end": v(-133.1, 9.65) * mm});
            skLineSegment(sketch, "E105.1", {"start": v(-130.05, 6.6) * mm, "end": v(-130.05, -6.6) * mm});
            skLineSegment(sketch, "E105.2", {"start": v(-133.1, 9.65) * mm, "end": v(-146.3, 9.65) * mm});
            skArc(sketch, "E105.3", {"start": v(-133.1, -9.65) * mm, "mid": v(-130.94, -8.76) * mm, "end": v(-130.05, -6.6) * mm});
            skArc(sketch, "E105.4", {"start": v(-146.3, 9.65) * mm, "mid": v(-148.46, 8.76) * mm, "end": v(-149.35, 6.6) * mm});
            skLineSegment(sketch, "E105.5", {"start": v(-149.35, 6.6) * mm, "end": v(-149.35, -6.6) * mm});
            skArc(sketch, "E105.6", {"start": v(-149.35, -6.6) * mm, "mid": v(-148.46, -8.76) * mm, "end": v(-146.3, -9.65) * mm});
            skLineSegment(sketch, "E105.7", {"start": v(-133.1, -9.65) * mm, "end": v(-146.3, -9.65) * mm});
            skArc(sketch, "E106.MirrorCS", {"start": v(149.35, -6.6) * mm, "mid": v(148.46, -8.76) * mm, "end": v(146.3, -9.65) * mm});
            skLineSegment(sketch, "E107.MirrorCS", {"start": v(133.1, -9.65) * mm, "end": v(146.3, -9.65) * mm});
            skArc(sketch, "E108.MirrorCS", {"start": v(127, 6.6) * mm, "mid": v(128.79, 10.91) * mm, "end": v(133.1, 12.7) * mm});
            skLineSegment(sketch, "E109.MirrorCS", {"start": v(133.1, 9.65) * mm, "end": v(146.3, 9.65) * mm});
            skArc(sketch, "E110.MirrorCS", {"start": v(146.3, 9.65) * mm, "mid": v(148.46, 8.76) * mm, "end": v(149.35, 6.6) * mm});
            skPoint(sketch, "E111.MirrorP", {"position": v(127, 12.7) * mm});
            skLineSegment(sketch, "E112.MirrorCS", {"start": v(130.05, 6.6) * mm, "end": v(130.05, -6.6) * mm});
            skArc(sketch, "E113.MirrorCS", {"start": v(152.4, -6.6) * mm, "mid": v(150.61, -10.91) * mm, "end": v(146.3, -12.7) * mm});
            skArc(sketch, "E114.MirrorCS", {"start": v(133.1, -12.7) * mm, "mid": v(128.79, -10.91) * mm, "end": v(127, -6.6) * mm});
            skArc(sketch, "E115.MirrorCS", {"start": v(130.05, 6.6) * mm, "mid": v(130.94, 8.76) * mm, "end": v(133.1, 9.65) * mm});
            skLineSegment(sketch, "E116.MirrorCS", {"start": v(149.35, 6.6) * mm, "end": v(149.35, -6.6) * mm});
            skLineSegment(sketch, "E117.MirrorCS", {"start": v(133.1, -12.7) * mm, "end": v(146.3, -12.7) * mm});
            skArc(sketch, "E118.MirrorCS", {"start": v(133.1, -9.65) * mm, "mid": v(130.94, -8.76) * mm, "end": v(130.05, -6.6) * mm});
            skArc(sketch, "E119.MirrorCS", {"start": v(146.3, 12.7) * mm, "mid": v(150.61, 10.91) * mm, "end": v(152.4, 6.6) * mm});
            skLineSegment(sketch, "E120.MirrorCS", {"start": v(133.1, 12.7) * mm, "end": v(146.3, 12.7) * mm});
            skLineSegment(sketch, "E121.MirrorCS", {"start": v(127, 6.6) * mm, "end": v(127, -6.6) * mm});
            skPoint(sketch, "E122.MirrorP", {"position": v(152.4, -12.7) * mm});
            skPoint(sketch, "E123.MirrorP", {"position": v(139.7, 0) * mm});
            skLineSegment(sketch, "E124.MirrorCS", {"start": v(152.4, 6.6) * mm, "end": v(152.4, -6.6) * mm});
            skPoint(sketch, "E125.MirrorP", {"position": v(127, -12.7) * mm});
            skPoint(sketch, "E126.MirrorP", {"position": v(152.4, 12.7) * mm});
            skSolve(sketch);
        }
        {
            var Q0;
            Q0=makeQuery(id+"F15.imprint","IMPRINT",FACE,{"disambiguationData":[TD([[makeQuery(id+"F15.imprint","IMPRINT",EDGE,{"derivedFrom":sQuery(id+"F15.wireOp",EDGE,"E100.bottom")}),1.0]])]});
            var Q1;
            Q1=makeQuery(id+"F15.imprint","IMPRINT",FACE,{"disambiguationData":[TD([[makeQuery(id+"F15.imprint","IMPRINT",EDGE,{"derivedFrom":sQuery(id+"F15.wireOp",EDGE,"E106.MirrorCS")}),1.0]])]});
            extrude(context, id + "F16", {"entities" : qUnion([Q0, Q1]), "depth" : 762 * mm, "offsetDistance" : 25.4 * mm});
        }
        {
            var Q0;
            Q0=makeQuery(id+"F12.imprint","IMPRINT",FACE,{"disambiguationData":[TD([[makeQuery(id+"F12.imprint","IMPRINT",EDGE,{"derivedFrom":sQuery(id+"F12.wireOp",EDGE,"E90.MirrorCS")}),1.0]])]});
            var sketch = newSketch(context, id + "F17", { "sketchPlane" : qUnion([Q0])});
            skLineSegment(sketch, "E127", {"start": v(0, 127) * mm, "end": v(0, 152.4) * mm});
            skLineSegment(sketch, "E128", {"start": v(0, 152.4) * mm, "end": v(25.4, 127) * mm});
            skLineSegment(sketch, "E129", {"start": v(25.4, 127) * mm, "end": v(0, 127) * mm});
            skPoint(sketch, "E130", {"position": v(0, 139.7) * mm});
            skPoint(sketch, "E131", {"position": v(12.7, 127) * mm});
            skLineSegment(sketch, "E132", {"start": v(762, 127) * mm, "end": v(736.6, 127) * mm});
            skLineSegment(sketch, "E133", {"start": v(736.6, 127) * mm, "end": v(762, 152.4) * mm});
            skLineSegment(sketch, "E134", {"start": v(762, 152.4) * mm, "end": v(762, 127) * mm});
            skPoint(sketch, "E135", {"position": v(749.3, 127) * mm});
            skPoint(sketch, "E136", {"position": v(762, 139.7) * mm});
            skLineSegment(sketch, "E137.MirrorCS", {"start": v(762, -152.4) * mm, "end": v(762, -127) * mm});
            skLineSegment(sketch, "E138.MirrorCS", {"start": v(736.6, -127) * mm, "end": v(762, -152.4) * mm});
            skLineSegment(sketch, "E139.MirrorCS", {"start": v(762, -127) * mm, "end": v(736.6, -127) * mm});
            skLineSegment(sketch, "E140.MirrorCS", {"start": v(25.4, -127) * mm, "end": v(0, -127) * mm});
            skLineSegment(sketch, "E141.MirrorCS", {"start": v(0, -152.4) * mm, "end": v(25.4, -127) * mm});
            skLineSegment(sketch, "E142.MirrorCS", {"start": v(0, -127) * mm, "end": v(0, -152.4) * mm});
            skPoint(sketch, "E143.MirrorP", {"position": v(0, -139.7) * mm});
            skPoint(sketch, "E144.MirrorP", {"position": v(762, -139.7) * mm});
            skPoint(sketch, "E145.MirrorP", {"position": v(749.3, -127) * mm});
            skPoint(sketch, "E146.MirrorP", {"position": v(12.7, -127) * mm});
            skSolve(sketch);
        }
        {
            var Q0;
            Q0=makeQuery(id+"F17.imprint","IMPRINT",FACE,{"disambiguationData":[TD([[makeQuery(id+"F17.imprint","IMPRINT",EDGE,{"derivedFrom":sQuery(id+"F17.wireOp",EDGE,"E127")}),-1.0]])]});
            var Q1;
            Q1=makeQuery(id+"F17.imprint","IMPRINT",FACE,{"disambiguationData":[TD([[makeQuery(id+"F17.imprint","IMPRINT",EDGE,{"derivedFrom":sQuery(id+"F17.wireOp",EDGE,"E140.MirrorCS")}),1.0]])]});
            var Q2;
            Q2=makeQuery(id+"F17.imprint","IMPRINT",FACE,{"disambiguationData":[TD([[makeQuery(id+"F17.imprint","IMPRINT",EDGE,{"derivedFrom":sQuery(id+"F17.wireOp",EDGE,"E137.MirrorCS")}),1.0]])]});
            var Q3;
            Q3=makeQuery(id+"F17.imprint","IMPRINT",FACE,{"disambiguationData":[TD([[makeQuery(id+"F17.imprint","IMPRINT",EDGE,{"derivedFrom":sQuery(id+"F17.wireOp",EDGE,"E132")}),-1.0]])]});
            extrude(context, id + "F18", {"entities" : qUnion([Q0, Q1, Q2, Q3]), "endBound" : BoundingType.SYMMETRIC, "depth" : 50.8 * mm, "offsetDistance" : 25.4 * mm});
        }
        {
            var Q0;
            Q0=makeQuery(id+"F18.opExtrude","SWEPT_BODY",BODY,{"disambiguationData":[OSD([sQuery(id+"F17.wireOp",EDGE,"E132"),sQuery(id+"F17.wireOp",EDGE,"E133"),sQuery(id+"F17.wireOp",EDGE,"E134")])]});
            var Q1;
            Q1=makeQuery(id+"F18.opExtrude","SWEPT_BODY",BODY,{"disambiguationData":[OSD([sQuery(id+"F17.wireOp",EDGE,"E127"),sQuery(id+"F17.wireOp",EDGE,"E128"),sQuery(id+"F17.wireOp",EDGE,"E129")])]});
            var Q2;
            Q2=makeQuery(id+"F18.opExtrude","SWEPT_BODY",BODY,{"disambiguationData":[OSD([sQuery(id+"F17.wireOp",EDGE,"E140.MirrorCS"),sQuery(id+"F17.wireOp",EDGE,"E141.MirrorCS"),sQuery(id+"F17.wireOp",EDGE,"E142.MirrorCS")])]});
            var Q3;
            Q3=makeQuery(id+"F18.opExtrude","SWEPT_BODY",BODY,{"disambiguationData":[OSD([sQuery(id+"F17.wireOp",EDGE,"E137.MirrorCS"),sQuery(id+"F17.wireOp",EDGE,"E138.MirrorCS"),sQuery(id+"F17.wireOp",EDGE,"E139.MirrorCS")])]});
            var Q4;
            Q4=makeQuery(id+"F16.opExtrude","SWEPT_BODY",BODY,{"disambiguationData":[OSD([sQuery(id+"F15.wireOp",EDGE,"E106.MirrorCS"),sQuery(id+"F15.wireOp",EDGE,"E107.MirrorCS"),sQuery(id+"F15.wireOp",EDGE,"E108.MirrorCS"),sQuery(id+"F15.wireOp",EDGE,"E109.MirrorCS"),sQuery(id+"F15.wireOp",EDGE,"E110.MirrorCS"),sQuery(id+"F15.wireOp",EDGE,"E112.MirrorCS"),sQuery(id+"F15.wireOp",EDGE,"E113.MirrorCS"),sQuery(id+"F15.wireOp",EDGE,"E114.MirrorCS"),sQuery(id+"F15.wireOp",EDGE,"E115.MirrorCS"),sQuery(id+"F15.wireOp",EDGE,"E116.MirrorCS"),sQuery(id+"F15.wireOp",EDGE,"E117.MirrorCS"),sQuery(id+"F15.wireOp",EDGE,"E118.MirrorCS"),sQuery(id+"F15.wireOp",EDGE,"E119.MirrorCS"),sQuery(id+"F15.wireOp",EDGE,"E120.MirrorCS"),sQuery(id+"F15.wireOp",EDGE,"E121.MirrorCS"),sQuery(id+"F15.wireOp",EDGE,"E124.MirrorCS")])]});
            var Q5;
            Q5=makeQuery(id+"F16.opExtrude","SWEPT_BODY",BODY,{"disambiguationData":[OSD([sQuery(id+"F15.wireOp",EDGE,"E100.bottom"),sQuery(id+"F15.wireOp",EDGE,"E100.top"),sQuery(id+"F15.wireOp",EDGE,"E100.left"),sQuery(id+"F15.wireOp",EDGE,"E100.right"),sQuery(id+"F15.wireOp",EDGE,"E101.filletArc"),sQuery(id+"F15.wireOp",EDGE,"E102.filletArc"),sQuery(id+"F15.wireOp",EDGE,"E103.filletArc"),sQuery(id+"F15.wireOp",EDGE,"E104.filletArc"),sQuery(id+"F15.wireOp",EDGE,"E105.0"),sQuery(id+"F15.wireOp",EDGE,"E105.1"),sQuery(id+"F15.wireOp",EDGE,"E105.2"),sQuery(id+"F15.wireOp",EDGE,"E105.3"),sQuery(id+"F15.wireOp",EDGE,"E105.4"),sQuery(id+"F15.wireOp",EDGE,"E105.5"),sQuery(id+"F15.wireOp",EDGE,"E105.6"),sQuery(id+"F15.wireOp",EDGE,"E105.7")])]});
            booleanBodies(context, id + "F19", {"operationType" : BooleanOperationType.SUBTRACTION, "tools" : qUnion([Q0, Q1, Q2, Q3]), "targets" : qUnion([Q4, Q5])});
        }
        {
            var Q0;
            Q0=qCreatedBy(makeId("Top.planeOp"),FACE);
            var sketch = newSketch(context, id + "F20", { "sketchPlane" : qUnion([Q0])});
            skCircle(sketch, "E147", {"center": v(-368.3, -139.7) * mm, "radius": 13.34 * mm});
            skCircle(sketch, "E148", {"center": v(-368.3, -139.7) * mm, "radius": 9.53 * mm});
            skLineSegment(sketch, "E149.bottom", {"start": v(-393.7, 165.1) * mm, "end": v(393.7, 165.1) * mm, "construction": true});
            skLineSegment(sketch, "E149.top", {"start": v(-393.7, -165.1) * mm, "end": v(393.7, -165.1) * mm, "construction": true});
            skLineSegment(sketch, "E149.left", {"start": v(-393.7, 165.1) * mm, "end": v(-393.7, -165.1) * mm, "construction": true});
            skLineSegment(sketch, "E149.right", {"start": v(393.7, 165.1) * mm, "end": v(393.7, -165.1) * mm, "construction": true});
            skLineSegment(sketch, "E150", {"start": v(-393.7, 165.1) * mm, "end": v(393.7, -165.1) * mm, "construction": true});
            skLineSegment(sketch, "E151", {"start": v(393.7, 165.1) * mm, "end": v(-393.7, -165.1) * mm, "construction": true});
            skPoint(sketch, "E152", {"position": v(0, 0) * mm});
            skLineSegment(sketch, "E153.bottom", {"start": v(-355.6, 127) * mm, "end": v(355.6, 127) * mm, "construction": true});
            skLineSegment(sketch, "E153.top", {"start": v(-355.6, -127) * mm, "end": v(355.6, -127) * mm, "construction": true});
            skLineSegment(sketch, "E153.left", {"start": v(-355.6, 127) * mm, "end": v(-355.6, -127) * mm, "construction": true});
            skLineSegment(sketch, "E153.right", {"start": v(355.6, 127) * mm, "end": v(355.6, -127) * mm, "construction": true});
            skLineSegment(sketch, "E154", {"start": v(-355.6, 127) * mm, "end": v(355.6, -127) * mm, "construction": true});
            skLineSegment(sketch, "E155", {"start": v(355.6, 127) * mm, "end": v(-355.6, -127) * mm, "construction": true});
            skLineSegment(sketch, "E156.bottom", {"start": v(-381, 152.4) * mm, "end": v(381, 152.4) * mm, "construction": true});
            skLineSegment(sketch, "E156.top", {"start": v(-381, -152.4) * mm, "end": v(381, -152.4) * mm, "construction": true});
            skLineSegment(sketch, "E156.left", {"start": v(-381, 152.4) * mm, "end": v(-381, -152.4) * mm, "construction": true});
            skLineSegment(sketch, "E156.right", {"start": v(381, 152.4) * mm, "end": v(381, -152.4) * mm, "construction": true});
            skLineSegment(sketch, "E157", {"start": v(-381, -152.4) * mm, "end": v(-355.6, -127) * mm, "construction": true});
            skCircle(sketch, "E158.MirrorC", {"center": v(368.3, -139.7) * mm, "radius": 13.34 * mm});
            skCircle(sketch, "E159.MirrorC", {"center": v(368.3, -139.7) * mm, "radius": 9.53 * mm});
            skCircle(sketch, "E160.MirrorC", {"center": v(-368.3, 139.7) * mm, "radius": 13.34 * mm});
            skCircle(sketch, "E161.MirrorC", {"center": v(-368.3, 139.7) * mm, "radius": 9.53 * mm});
            skCircle(sketch, "E162.MirrorC", {"center": v(368.3, 139.7) * mm, "radius": 13.34 * mm});
            skCircle(sketch, "E163.MirrorC", {"center": v(368.3, 139.7) * mm, "radius": 9.53 * mm});
            skSolve(sketch);
        }
        {
            var Q0;
            Q0=makeQuery(id+"F20.imprint","IMPRINT",FACE,{"disambiguationData":[TD([[makeQuery(id+"F20.imprint","IMPRINT",EDGE,{"derivedFrom":sQuery(id+"F20.wireOp",EDGE,"E160.MirrorC")}),-1.0]])]});
            var Q1;
            Q1=makeQuery(id+"F20.imprint","IMPRINT",FACE,{"disambiguationData":[TD([[makeQuery(id+"F20.imprint","IMPRINT",EDGE,{"derivedFrom":sQuery(id+"F20.wireOp",EDGE,"E147")}),1.0]])]});
            var Q2;
            Q2=makeQuery(id+"F20.imprint","IMPRINT",FACE,{"disambiguationData":[TD([[makeQuery(id+"F20.imprint","IMPRINT",EDGE,{"derivedFrom":sQuery(id+"F20.wireOp",EDGE,"E158.MirrorC")}),-1.0]])]});
            var Q3;
            Q3=makeQuery(id+"F20.imprint","IMPRINT",FACE,{"disambiguationData":[TD([[makeQuery(id+"F20.imprint","IMPRINT",EDGE,{"derivedFrom":sQuery(id+"F20.wireOp",EDGE,"E162.MirrorC")}),1.0]])]});
            extrude(context, id + "F21", {"entities" : qUnion([Q0, Q1, Q2, Q3]), "depth" : 76.2 * mm, "offsetDistance" : 25.4 * mm});
        }
        {
            var Q0;
            Q0=makeQuery(id+"F20.imprint","IMPRINT",FACE,{"disambiguationData":[TD([[makeQuery(id+"F20.imprint","IMPRINT",EDGE,{"derivedFrom":sQuery(id+"F20.wireOp",EDGE,"E148")}),1.0]])]});
            var Q1;
            Q1=makeQuery(id+"F20.imprint","IMPRINT",FACE,{"disambiguationData":[TD([[makeQuery(id+"F20.imprint","IMPRINT",EDGE,{"derivedFrom":sQuery(id+"F20.wireOp",EDGE,"E161.MirrorC")}),-1.0]])]});
            var Q2;
            Q2=makeQuery(id+"F20.imprint","IMPRINT",FACE,{"disambiguationData":[TD([[makeQuery(id+"F20.imprint","IMPRINT",EDGE,{"derivedFrom":sQuery(id+"F20.wireOp",EDGE,"E163.MirrorC")}),1.0]])]});
            var Q3;
            Q3=makeQuery(id+"F20.imprint","IMPRINT",FACE,{"disambiguationData":[TD([[makeQuery(id+"F20.imprint","IMPRINT",EDGE,{"derivedFrom":sQuery(id+"F20.wireOp",EDGE,"E159.MirrorC")}),-1.0]])]});
            extrude(context, id + "F22", {"entities" : qUnion([Q0, Q1, Q2, Q3]), "depth" : 127 * mm, "offsetDistance" : 25.4 * mm});
        }
        {
            var Q0;
            Q0=makeQuery(id+"F10.imprint","IMPRINT",FACE,{"disambiguationData":[TD([[makeQuery(id+"F10.imprint","IMPRINT",EDGE,{"derivedFrom":sQuery(id+"F10.wireOp",EDGE,"E57.bottom")}),1.0]])]});
            extrude(context, id + "F23", {"entities" : qUnion([Q0]), "depth" : 254 * mm, "offsetDistance" : 25.4 * mm});
        }
    });
